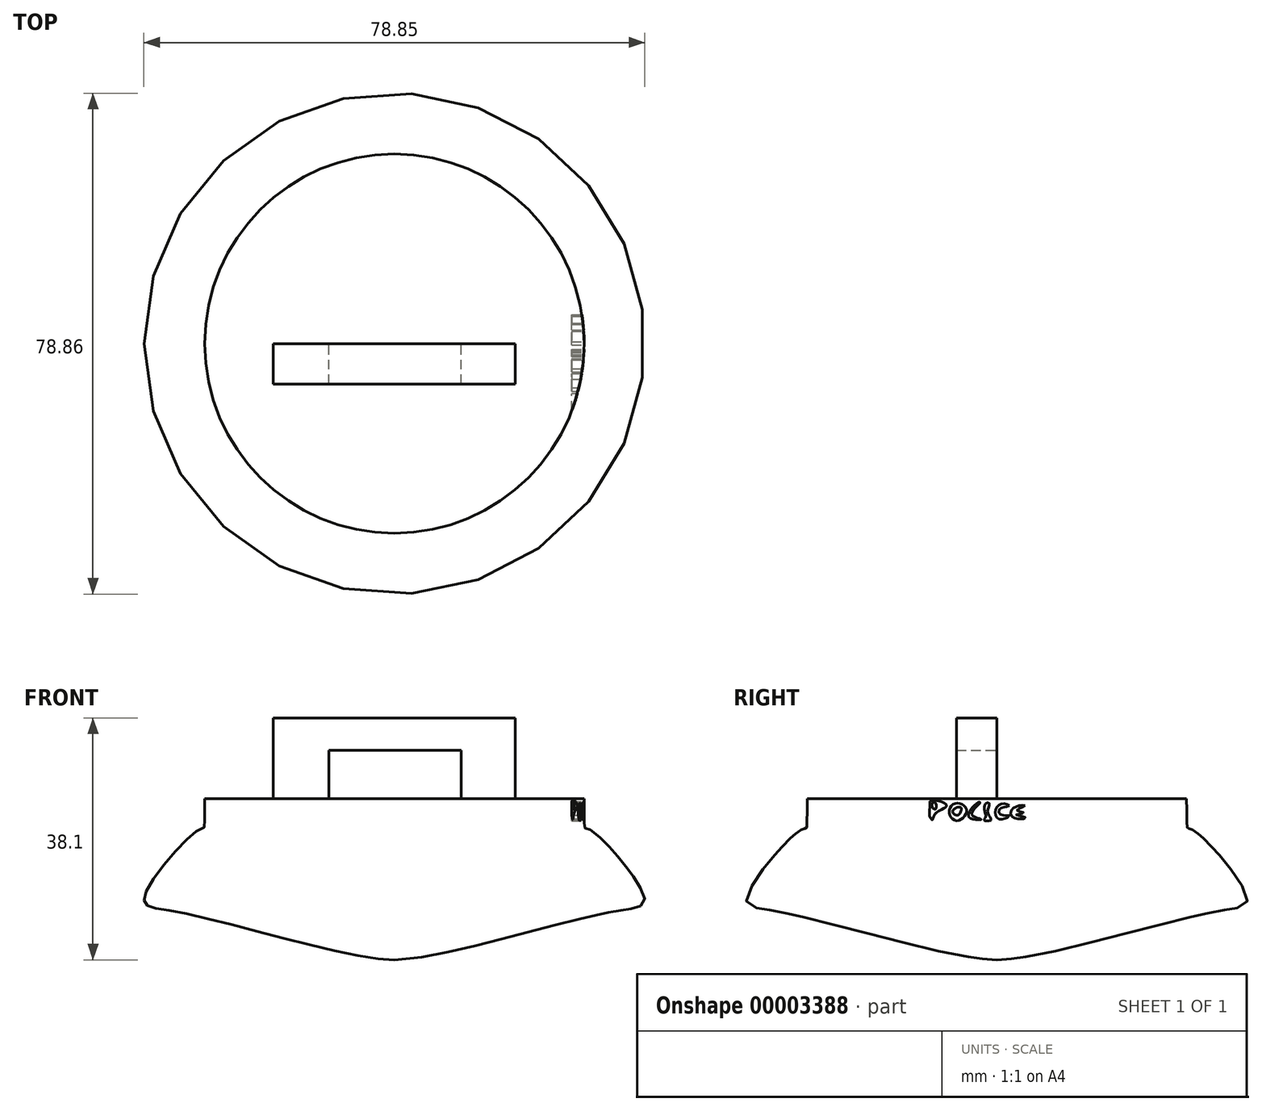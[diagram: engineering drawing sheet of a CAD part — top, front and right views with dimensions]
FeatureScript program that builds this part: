
annotation { "Feature Type Name" : "Feature", "Feature Type Description" : "" }
export const myFeature = defineFeature(function(context is Context, id is Id, definition is map)
    precondition{}
    {
        {
            var Q0;
            Q0=qCreatedBy(makeId("Front.planeOp"),FACE);
            var sketch = newSketch(context, id + "F0", { "sketchPlane" : qUnion([Q0])});
            skFitSpline(sketch, "E0", {"points": [v(-29.85, 0) * mm, v(-30.77, -4.9) * mm, v(-39.39, -15.6) * mm, v(-34.58, -17.78) * mm, v(0, -25.4) * mm], "startDerivative": vector(-2.24, -112.8) * mm, "endDerivative": vector(51.25, -0.05) * mm});
            skLineSegment(sketch, "E1", {"start": v(-29.85, 0) * mm, "end": v(0, 0) * mm});
            skLineSegment(sketch, "E2", {"start": v(0, 0) * mm, "end": v(0, -25.4) * mm});
            skSolve(sketch);
        }
        {
            var Q0;
            Q0=qCreatedBy(makeId("Front.planeOp"),FACE);
            var sketch = newSketch(context, id + "F1", { "sketchPlane" : qUnion([Q0])});
            skLineSegment(sketch, "E3", {"start": v(0, 38.14) * mm, "end": v(0, -46.32) * mm});
            skSolve(sketch);
        }
        {
            var Q0;
            Q0=makeQuery(id+"F0.imprint","IMPRINT",FACE,{"disambiguationData":[TD([[makeQuery(id+"F0.imprint","IMPRINT",EDGE,{"derivedFrom":sQuery(id+"F0.wireOp",EDGE,"E0")}),1.0]])]});
            var Q1;
            {var subQ0=sQuery(id+"F0.wireOp",EDGE,"7daf59d7-36d5-40c3-b46c-32f78c155582");Q1=makeQuery(id+"F0.imprint","IMPRINT",FACE,{"disambiguationData":[TD([[makeQuery(id+"F0.imprint","IMPRINT",EDGE,{"derivedFrom":subQ0}),1.0]])]});}
            var Q2;
            {var subQ1=sQuery(id+"F0.wireOp",EDGE,"db690256-2e2c-4568-aae6-5ea2a57716da");Q2=makeQuery(id+"F0.imprint","IMPRINT",FACE,{"disambiguationData":[TD([[makeQuery(id+"F0.imprint","IMPRINT",EDGE,{"derivedFrom":subQ1}),1.0]])]});}
            var Q3;
            Q3=sQuery(id+"F1.wireOp",EDGE,"E3");
            revolve(context, id + "F2", {"entities" : qUnion([Q0, Q1, Q2]), "axis" : qUnion([Q3]), "revolveType" : RevolveType.FULL});
        }
        {
            var Q0;
            Q0=qCreatedBy(makeId("Right.planeOp"),FACE);
            cPlane(context, id + "F3", {"entities" : qUnion([Q0]), "cplaneType" : CPlaneType.OFFSET, "offset" : 27.94 * mm, "width" : 152.4 * mm, "height" : 152.4 * mm});
        }
        {
            var Q0;
            Q0=qCreatedBy(id+"F3.planeOp",FACE);
            var sketch = newSketch(context, id + "F4", { "sketchPlane" : qUnion([Q0])});
            skFitSpline(sketch, "E4", {"points": [v(-10.23, -3.34) * mm, v(-10.74, -0.55) * mm, v(-7.93, -1.06) * mm, v(-9.7, -2.4) * mm, v(-10.23, -3.34) * mm]});
            skFitSpline(sketch, "E5", {"points": [v(-10.23, -1) * mm, v(-9.7, -0.66) * mm, v(-9.7, -1.68) * mm, v(-10.23, -1) * mm]});
            skFitSpline(sketch, "E6", {"points": [v(-6.33, -3.5) * mm, v(-7.5, -2.04) * mm, v(-6.3, -0.72) * mm, v(-4.75, -1.9) * mm, v(-6.33, -3.5) * mm]});
            skFitSpline(sketch, "E7", {"points": [v(-6.55, -2.6) * mm, v(-6.93, -1.9) * mm, v(-5.7, -1.4) * mm, v(-5.85, -2.38) * mm, v(-6.55, -2.6) * mm]});
            skFitSpline(sketch, "E8", {"points": [v(-3.2, -0.77) * mm, v(-4.34, -3) * mm, v(-2.38, -3.26) * mm, v(-3.94, -2.54) * mm, v(-2.57, -0.56) * mm, v(-3.2, -0.77) * mm]});
            skFitSpline(sketch, "E9", {"points": [v(-1.78, -0.77) * mm, v(-1.86, -2.2) * mm, v(-1.78, -2.93) * mm, v(-2.02, -3.43) * mm, v(-0.92, -3.38) * mm, v(-1.43, -2.2) * mm, v(-1.19, -0.77) * mm, v(-1.78, -0.77) * mm]});
            skFitSpline(sketch, "E10", {"points": [v(1.95, -1.1) * mm, v(0.32, -0.99) * mm, v(0.23, -3.21) * mm, v(1.95, -2.73) * mm, v(0.6, -2.54) * mm, v(0.46, -1.63) * mm, v(1.95, -1.1) * mm]});
            skFitSpline(sketch, "E11", {"points": [v(4.46, -1.1) * mm, v(2.52, -1.56) * mm, v(2.64, -3.02) * mm, v(4.56, -3.02) * mm, v(3.05, -2.54) * mm, v(4.32, -2.26) * mm, v(3.2, -1.87) * mm, v(4.46, -1.1) * mm]});
            skSolve(sketch);
        }
        {
            var Q0;
            Q0=makeQuery(id+"F4.imprint","IMPRINT",FACE,{"disambiguationData":[TD([[makeQuery(id+"F4.imprint","IMPRINT",EDGE,{"derivedFrom":sQuery(id+"F4.wireOp",EDGE,"E4")}),-1.0]])]});
            var Q1;
            Q1=makeQuery(id+"F4.imprint","IMPRINT",FACE,{"disambiguationData":[TD([[makeQuery(id+"F4.imprint","IMPRINT",EDGE,{"derivedFrom":sQuery(id+"F4.wireOp",EDGE,"E6")}),-1.0]])]});
            var Q2;
            Q2=makeQuery(id+"F4.imprint","IMPRINT",FACE,{"disambiguationData":[TD([[makeQuery(id+"F4.imprint","IMPRINT",EDGE,{"derivedFrom":sQuery(id+"F4.wireOp",EDGE,"E8")}),1.0]])]});
            var Q3;
            Q3=makeQuery(id+"F4.imprint","IMPRINT",FACE,{"disambiguationData":[TD([[makeQuery(id+"F4.imprint","IMPRINT",EDGE,{"derivedFrom":sQuery(id+"F4.wireOp",EDGE,"E9")}),1.0]])]});
            var Q4;
            Q4=makeQuery(id+"F4.imprint","IMPRINT",FACE,{"disambiguationData":[TD([[makeQuery(id+"F4.imprint","IMPRINT",EDGE,{"derivedFrom":sQuery(id+"F4.wireOp",EDGE,"E10")}),1.0]])]});
            var Q5;
            Q5=makeQuery(id+"F4.imprint","IMPRINT",FACE,{"disambiguationData":[TD([[makeQuery(id+"F4.imprint","IMPRINT",EDGE,{"derivedFrom":sQuery(id+"F4.wireOp",EDGE,"E11")}),1.0]])]});
            var Q6;
            Q6=makeQuery(id+"F2.opRevolve","SWEPT_FACE",FACE,{"disambiguationData":[OSD([sQuery(id+"F0.wireOp",EDGE,"E0")])]});
            extrude(context, id + "F5", {"entities" : qUnion([Q0, Q1, Q2, Q3, Q4, Q5]), "operationType" : NewBodyOperationType.REMOVE, "endBound" : BoundingType.UP_TO_SURFACE, "endBoundEntityFace" : qUnion([Q6]), "depth" : 25.4 * mm});
        }
        {
            var Q0;
            Q0=makeQuery(id+"F2.opRevolve","SWEPT_FACE",FACE,{"disambiguationData":[OSD([sQuery(id+"F0.wireOp",EDGE,"E1")])]});
            var sketch = newSketch(context, id + "F6", { "sketchPlane" : qUnion([Q0])});
            skLineSegment(sketch, "E12.bottom", {"start": v(-1.59, -12.7) * mm, "end": v(1.59, -12.7) * mm});
            skLineSegment(sketch, "E12.top", {"start": v(-1.59, 12.7) * mm, "end": v(1.59, 12.7) * mm});
            skLineSegment(sketch, "E12.left", {"start": v(-1.59, -12.7) * mm, "end": v(-1.59, 12.7) * mm});
            skLineSegment(sketch, "E12.right", {"start": v(1.59, -12.7) * mm, "end": v(1.59, 12.7) * mm});
            skSolve(sketch);
        }
        {
            var Q0;
            Q0=qCreatedBy(makeId("Front.planeOp"),FACE);
            var sketch = newSketch(context, id + "F7", { "sketchPlane" : qUnion([Q0])});
            skLineSegment(sketch, "E13.bottom", {"start": v(0, 0) * mm, "end": v(-19.05, 0) * mm});
            skLineSegment(sketch, "E13.top", {"start": v(0, 12.7) * mm, "end": v(-19.05, 12.7) * mm});
            skLineSegment(sketch, "E13.right", {"start": v(-19.05, 0) * mm, "end": v(-19.05, 12.7) * mm});
            skLineSegment(sketch, "E14.0.MirrorCS", {"start": v(0, 12.7) * mm, "end": v(19.05, 12.7) * mm});
            skLineSegment(sketch, "E15.0.MirrorCS", {"start": v(19.05, 0) * mm, "end": v(19.05, 12.7) * mm});
            skLineSegment(sketch, "E16", {"start": v(0, 0) * mm, "end": v(19.05, 0) * mm});
            skSolve(sketch);
        }
        {
            var Q0;
            Q0 = qSketchRegion(id + "F7", true);
            extrude(context, id + "F8", {"entities" : qUnion([Q0]), "operationType" : NewBodyOperationType.ADD, "depth" : 6.35 * mm});
        }
        {
            var Q0;
            Q0=makeQuery(id+"F8.opExtrude","CAP_FACE",FACE,{"disambiguationData":[OSD([sQuery(id+"F7.wireOp",EDGE,"E13.bottom"),sQuery(id+"F7.wireOp",EDGE,"E13.right"),sQuery(id+"F7.wireOp",EDGE,"E14.0.MirrorCS"),sQuery(id+"F7.wireOp",EDGE,"E15.0.MirrorCS")])],"isStart":true});
            var sketch = newSketch(context, id + "F9", { "sketchPlane" : qUnion([Q0])});
            skLineSegment(sketch, "E17.left", {"start": v(-10.52, 0) * mm, "end": v(-10.52, 7.62) * mm});
            skLineSegment(sketch, "E17.right", {"start": v(10.31, 0) * mm, "end": v(10.31, 7.62) * mm});
            skLineSegment(sketch, "E18", {"start": v(10.31, 7.62) * mm, "end": v(-10.52, 7.62) * mm});
            skLineSegment(sketch, "E19", {"start": v(-10.52, 0) * mm, "end": v(0, 0) * mm});
            skLineSegment(sketch, "E20.0.MirrorCS", {"start": v(10.52, 0) * mm, "end": v(0, 0) * mm});
            skSolve(sketch);
        }
        {
            var Q0;
            Q0 = qSketchRegion(id + "F9", true);
            extrude(context, id + "F10", {"entities" : qUnion([Q0]), "operationType" : NewBodyOperationType.REMOVE, "oppositeDirection" : true, "depth" : 25.4 * mm});
        }
    });
